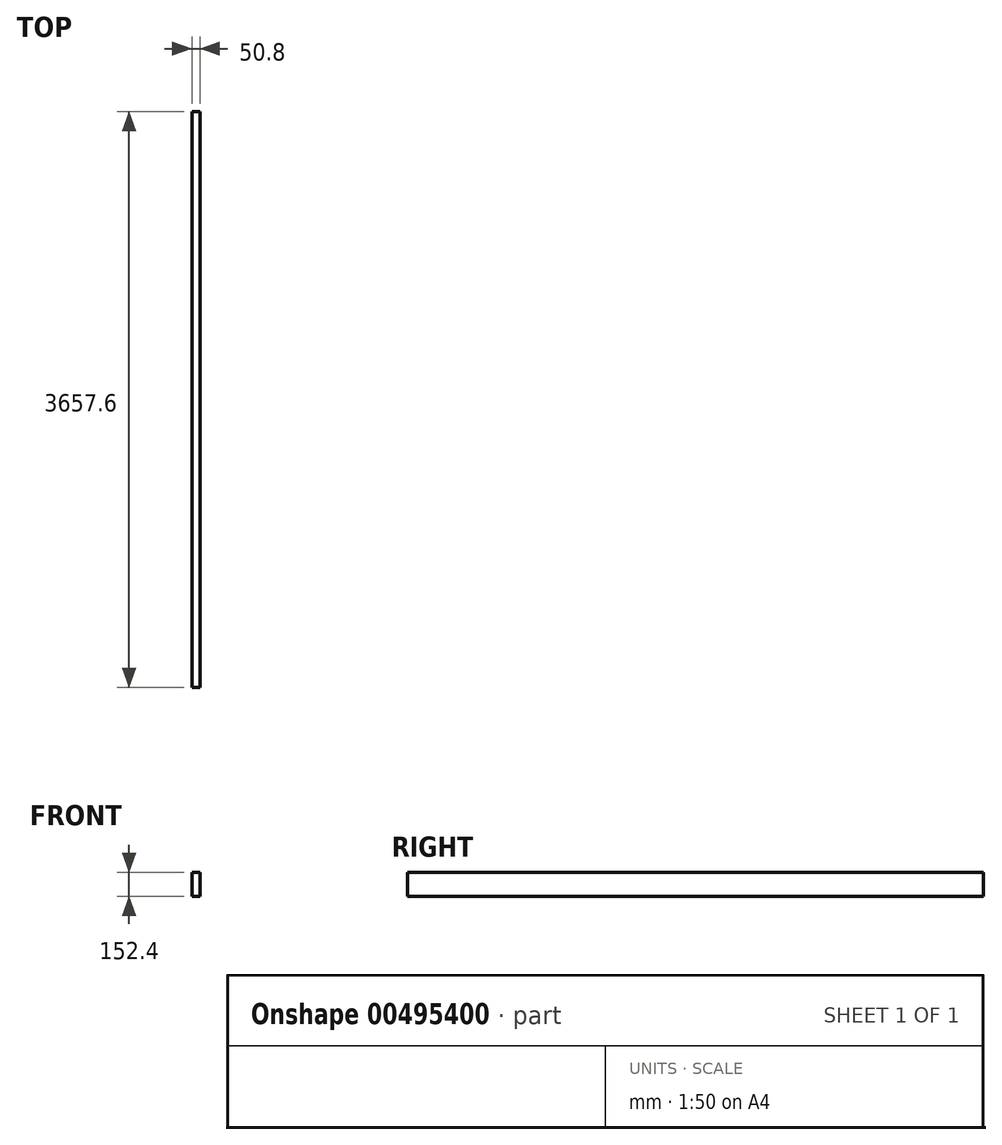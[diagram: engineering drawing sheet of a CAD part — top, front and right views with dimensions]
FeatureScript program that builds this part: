
annotation { "Feature Type Name" : "Feature", "Feature Type Description" : "" }
export const myFeature = defineFeature(function(context is Context, id is Id, definition is map)
    precondition{}
    {
        {
            var Q0;
            Q0=qCreatedBy(makeId("Front.planeOp"),FACE);
            var sketch = newSketch(context, id + "F0", { "sketchPlane" : qUnion([Q0])});
            skLineSegment(sketch, "E0.bottom", {"start": v(0, 0) * mm, "end": v(50.8, 0) * mm});
            skLineSegment(sketch, "E0.top", {"start": v(0, 152.4) * mm, "end": v(50.8, 152.4) * mm});
            skLineSegment(sketch, "E0.left", {"start": v(0, 0) * mm, "end": v(0, 152.4) * mm});
            skLineSegment(sketch, "E0.right", {"start": v(50.8, 0) * mm, "end": v(50.8, 152.4) * mm});
            skSolve(sketch);
        }
        {
            var Q0;
            Q0 = qSketchRegion(id + "F0", true);
            extrude(context, id + "F1", {"entities" : qUnion([Q0]), "depth" : 3657.6 * mm, "offsetDistance" : 25.4 * mm});
        }
    });
